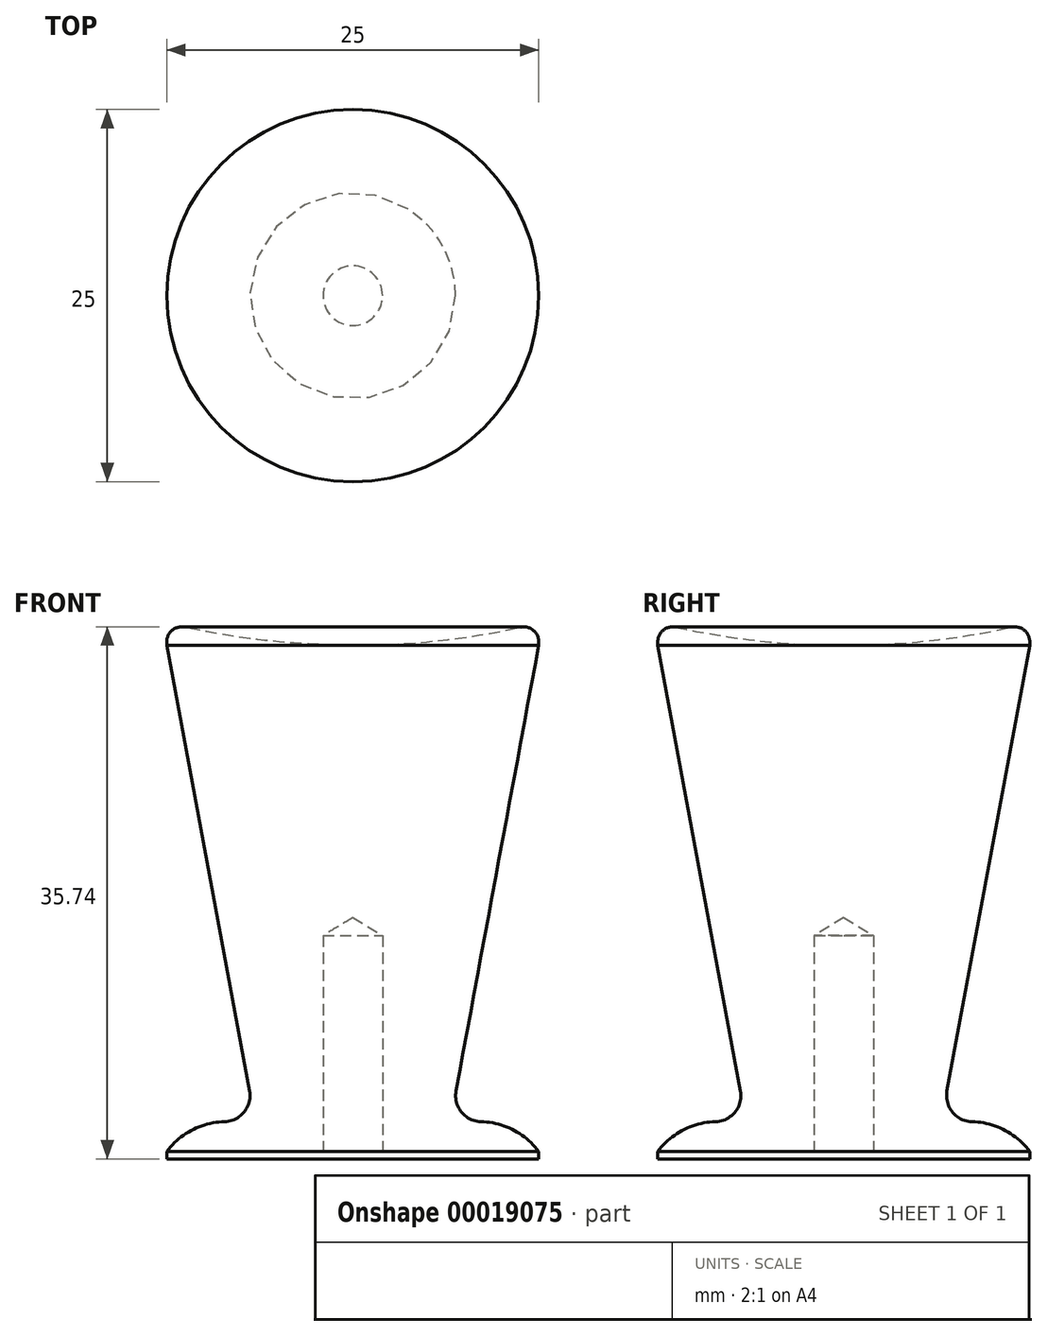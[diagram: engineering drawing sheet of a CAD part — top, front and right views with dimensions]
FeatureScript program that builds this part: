
annotation { "Feature Type Name" : "Feature", "Feature Type Description" : "" }
export const myFeature = defineFeature(function(context is Context, id is Id, definition is map)
    precondition{}
    {
        {
            var Q0;
            Q0=qCreatedBy(makeId("Front.planeOp"),FACE);
            var sketch = newSketch(context, id + "F0", { "sketchPlane" : qUnion([Q0])});
            skLineSegment(sketch, "E0", {"start": v(0, 0) * mm, "end": v(-12.5, 0) * mm});
            skLineSegment(sketch, "E1", {"start": v(-12.5, 0) * mm, "end": v(-12.5, 1.5) * mm});
            skArc(sketch, "E2", {"start": v(-8.66, 2) * mm, "mid": v(-10.6, 1.87) * mm, "end": v(-12.5, 1.5) * mm});
            skArc(sketch, "E3", {"start": v(-8.66, 2) * mm, "mid": v(-7.31, 2.63) * mm, "end": v(-6.94, 4.07) * mm});
            skLineSegment(sketch, "E4", {"start": v(-6.94, 4.07) * mm, "end": v(-12.5, 34) * mm});
            skLineSegment(sketch, "E5", {"start": v(-12.5, 34) * mm, "end": v(-12.5, 35.5) * mm});
            skLineSegment(sketch, "E6", {"start": v(-12.5, 35.5) * mm, "end": v(0, 35.5) * mm, "construction": true});
            skLineSegment(sketch, "E7", {"start": v(0, 34) * mm, "end": v(0, 0) * mm});
            skLineSegment(sketch, "E8", {"start": v(-8.66, 2) * mm, "end": v(0, 2) * mm, "construction": true});
            skArc(sketch, "E9", {"start": v(-12.5, 35.5) * mm, "mid": v(-6.3, 34.38) * mm, "end": v(0, 34) * mm});
            skLineSegment(sketch, "E10", {"start": v(0, 34) * mm, "end": v(-8.36, 34) * mm, "construction": true});
            skSolve(sketch);
        }
        {
            var Q0;
            Q0=makeQuery(id+"F0.imprint","IMPRINT",FACE,{"disambiguationData":[TD([[makeQuery(id+"F0.imprint","IMPRINT",EDGE,{"derivedFrom":sQuery(id+"F0.wireOp",EDGE,"E0")}),-1.0]])]});
            var Q1;
            Q1=sQuery(id+"F0.wireOp",EDGE,"E7");
            revolve(context, id + "F1", {"entities" : qUnion([Q0]), "axis" : qUnion([Q1]), "revolveType" : RevolveType.FULL});
        }
        {
            var Q0;
            Q0=makeQuery(id+"F1.opRevolve","SWEPT_EDGE",EDGE,{"disambiguationData":[OSD([sQuery(id+"F0.wireOp",EDGE,"E5"),sQuery(id+"F0.wireOp",EDGE,"E9")])]});
            fillet(context, id + "F2", {"entities" : qUnion([Q0]), "radius" : 1 * mm, "tangentPropagation" : true, "allowEdgeOverflow" : false});
        }
        {
            var Q0;
            Q0=makeQuery(id+"F1.opRevolve","SWEPT_EDGE",EDGE,{"disambiguationData":[OSD([sQuery(id+"F0.wireOp",EDGE,"E1"),sQuery(id+"F0.wireOp",EDGE,"E2")])]});
            fillet(context, id + "F3", {"entities" : qUnion([Q0]), "radius" : 5 * mm, "tangentPropagation" : true, "allowEdgeOverflow" : false});
        }
        {
            var Q0;
            Q0=makeQuery(id+"F1.opRevolve","SWEPT_FACE",FACE,{"disambiguationData":[OSD([sQuery(id+"F0.wireOp",EDGE,"E0")])]});
            var sketch = newSketch(context, id + "F4", { "sketchPlane" : qUnion([Q0])});
            skCircle(sketch, "E11.0.0", {"center": v(0, 0) * mm, "radius": 12.5 * mm});
            skSolve(sketch);
        }
        {
            var Q0;
            Q0 = qSketchRegion(id + "F4", true);
            var Q1;
            Q1=makeQuery(id+"F1.opRevolve","SWEPT_FACE",FACE,{"disambiguationData":[OSD([sQuery(id+"F0.wireOp",EDGE,"E0")])]});
            extrude(context, id + "F5", {"entities" : qUnion([Q0, Q1]), "operationType" : NewBodyOperationType.ADD, "depth" : .5 * mm});
        }
        {
            var Q0;
            Q0=makeQuery(id+"F5.opExtrude","CAP_FACE",FACE,{"disambiguationData":[OSD([sQuery(id+"F0.wireOp",EDGE,"E0")])],"isStart":false});
            var sketch = newSketch(context, id + "F6", { "sketchPlane" : qUnion([Q0])});
            skPoint(sketch, "E12", {"position": v(0, 0) * mm});
            skSolve(sketch);
        }
        {
            var Q0;
            Q0=sQuery(id+"F6.wireOp",VERTEX,"E12");
            var Q1;
            Q1=makeQuery(id+"F1.opRevolve","SWEPT_BODY",BODY,{"disambiguationData":[OSD([sQuery(id+"F0.wireOp",EDGE,"E0"),sQuery(id+"F0.wireOp",EDGE,"E1"),sQuery(id+"F0.wireOp",EDGE,"E2"),sQuery(id+"F0.wireOp",EDGE,"E3"),sQuery(id+"F0.wireOp",EDGE,"E4"),sQuery(id+"F0.wireOp",EDGE,"E5"),sQuery(id+"F0.wireOp",EDGE,"E6"),sQuery(id+"F0.wireOp",EDGE,"E7")])]});
            hole(context, id + "F7", {"style" : HoleStyle.SIMPLE, "holeDiameter" : 4 * mm, "endStyle" : HoleEndStyle.BLIND, "holeDepth" : 15 * mm, "locations" : qUnion([Q0]), "scope" : qUnion([Q1])});
        }
    });
